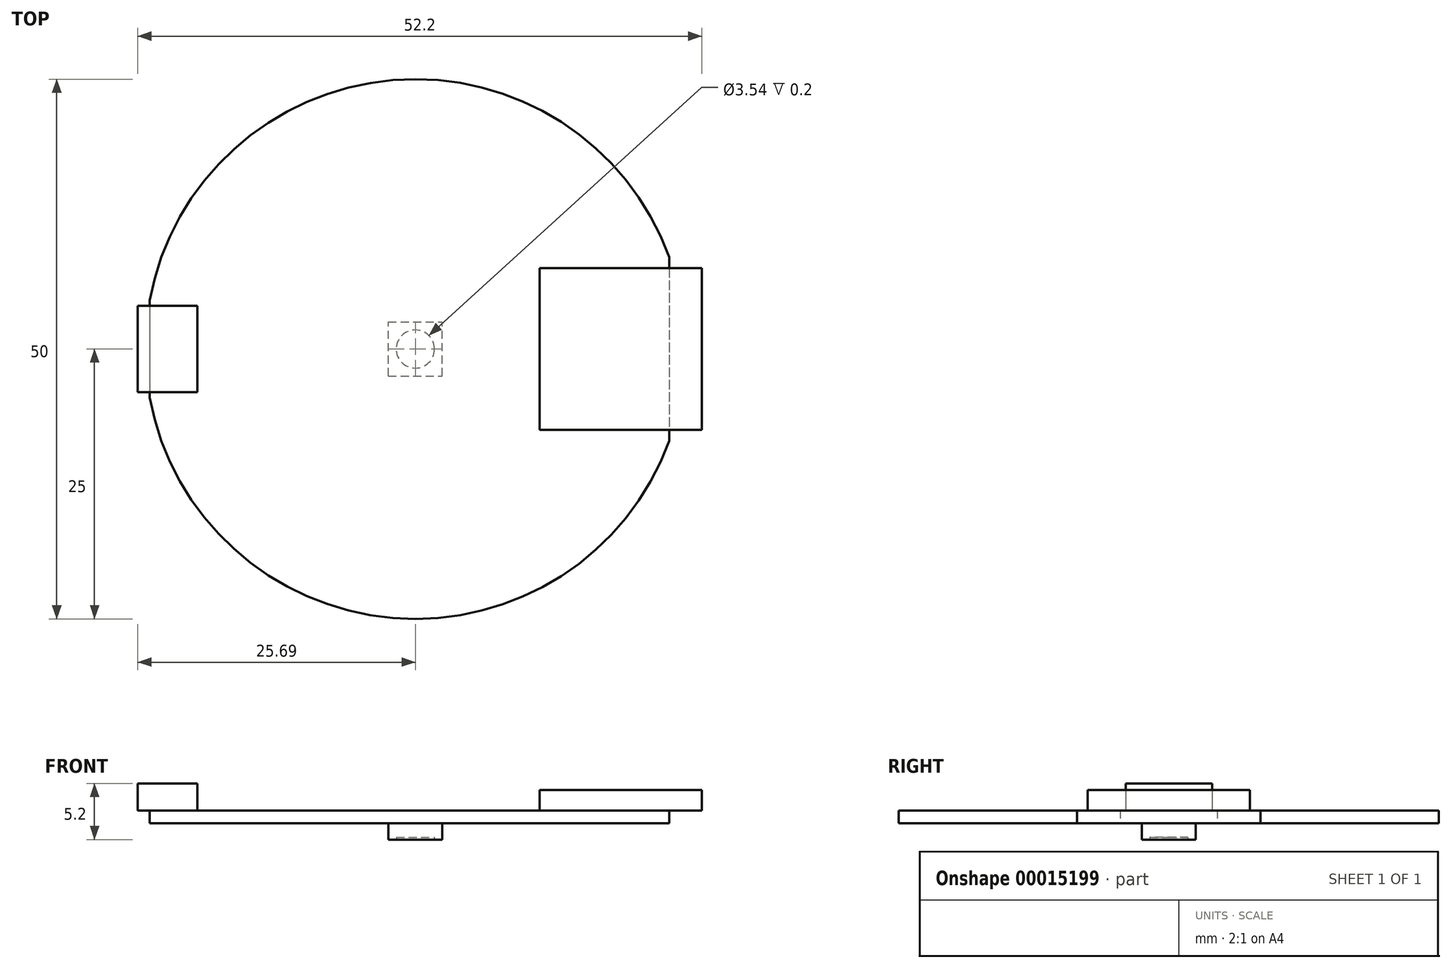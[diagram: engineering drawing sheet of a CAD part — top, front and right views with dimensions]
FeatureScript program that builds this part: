
annotation { "Feature Type Name" : "Feature", "Feature Type Description" : "" }
export const myFeature = defineFeature(function(context is Context, id is Id, definition is map)
    precondition{}
    {
        {
            var Q0;
            Q0=qCreatedBy(makeId("Top.planeOp"),FACE);
            var sketch = newSketch(context, id + "F0", { "sketchPlane" : qUnion([Q0])});
            skCircle(sketch, "E0", {"center": v(0, 0) * mm, "radius": 25 * mm});
            skLineSegment(sketch, "E1", {"start": v(23.51, 8.5) * mm, "end": v(23.51, -8.5) * mm});
            skLineSegment(sketch, "E2", {"start": v(-24.6, 4.5) * mm, "end": v(-24.6, -4.5) * mm});
            skSolve(sketch);
        }
        {
            var Q0;
            {var subQ0=sQuery(id+"F0.wireOp",EDGE,"E1");Q0=makeQuery(id+"F0.imprint","IMPRINT",FACE,{"disambiguationData":[TD([[makeQuery(id+"F0.imprint","IMPRINT",EDGE,{"derivedFrom":subQ0}),-1.0]])]});}
            extrude(context, id + "F1", {"entities" : qUnion([Q0]), "depth" : 1.2 * mm});
        }
        {
            var Q0;
            Q0=makeQuery(id+"F1.opExtrude","CAP_FACE",FACE,{"disambiguationData":[OSD([sQuery(id+"F0.wireOp",EDGE,"E0"),sQuery(id+"F0.wireOp",EDGE,"E1"),sQuery(id+"F0.wireOp",EDGE,"E2")])],"isStart":false});
            var sketch = newSketch(context, id + "F2", { "sketchPlane" : qUnion([Q0])});
            skLineSegment(sketch, "E3", {"start": v(0, 0) * mm, "end": v(-54.47, 0) * mm, "construction": true});
            skLineSegment(sketch, "E4.rect.bottom", {"start": v(-25.7, -4) * mm, "end": v(-20.2, -4) * mm});
            skLineSegment(sketch, "E4.rect.top", {"start": v(-25.7, 4) * mm, "end": v(-20.2, 4) * mm});
            skLineSegment(sketch, "E4.rect.left", {"start": v(-25.7, -4) * mm, "end": v(-25.7, 4) * mm});
            skLineSegment(sketch, "E4.rect.right", {"start": v(-20.2, -4) * mm, "end": v(-20.2, 4) * mm});
            skPoint(sketch, "E4.rect.middle", {"position": v(-22.94, 0) * mm});
            skPoint(sketch, "E5", {"position": v(-24.6, 0) * mm});
            skSolve(sketch);
        }
        {
            var Q0;
            Q0=qSketchRegion(id+"F2",true);
            extrude(context, id + "F3", {"entities" : qUnion([Q0]), "depth" : 2.5 * mm});
        }
        {
            var Q0;
            Q0=makeQuery(id+"F1.opExtrude","CAP_FACE",FACE,{"disambiguationData":[OSD([sQuery(id+"F0.wireOp",EDGE,"E0"),sQuery(id+"F0.wireOp",EDGE,"E1"),sQuery(id+"F0.wireOp",EDGE,"E2")])],"isStart":false});
            var sketch = newSketch(context, id + "F4", { "sketchPlane" : qUnion([Q0])});
            skLineSegment(sketch, "E6.bottom", {"start": v(26.51, -7.5) * mm, "end": v(11.51, -7.5) * mm});
            skLineSegment(sketch, "E6.top", {"start": v(26.51, 7.5) * mm, "end": v(11.51, 7.5) * mm});
            skLineSegment(sketch, "E6.left", {"start": v(26.51, -7.5) * mm, "end": v(26.51, 7.5) * mm});
            skLineSegment(sketch, "E6.right", {"start": v(11.51, -7.5) * mm, "end": v(11.51, 7.5) * mm});
            skLineSegment(sketch, "E7", {"start": v(0, 0) * mm, "end": v(28.6, 0) * mm, "construction": true});
            skSolve(sketch);
        }
        {
            var Q0;
            Q0=qSketchRegion(id+"F4",true);
            extrude(context, id + "F5", {"entities" : qUnion([Q0]), "depth" : 1.9 * mm});
        }
        {
            var Q0;
            Q0=makeQuery(id+"F1.opExtrude","CAP_FACE",FACE,{"disambiguationData":[OSD([sQuery(id+"F0.wireOp",EDGE,"E0"),sQuery(id+"F0.wireOp",EDGE,"E1"),sQuery(id+"F0.wireOp",EDGE,"E2")])],"isStart":true});
            var sketch = newSketch(context, id + "F6", { "sketchPlane" : qUnion([Q0])});
            skLineSegment(sketch, "E8.rect.bottom", {"start": v(-2.5, 2.5) * mm, "end": v(2.5, 2.5) * mm});
            skLineSegment(sketch, "E8.rect.top", {"start": v(-2.5, -2.5) * mm, "end": v(2.5, -2.5) * mm});
            skLineSegment(sketch, "E8.rect.left", {"start": v(-2.5, 2.5) * mm, "end": v(-2.5, -2.5) * mm});
            skLineSegment(sketch, "E8.rect.right", {"start": v(2.5, 2.5) * mm, "end": v(2.5, -2.5) * mm});
            skPoint(sketch, "E8.rect.middle", {"position": v(0, 0) * mm});
            skCircle(sketch, "E9", {"center": v(0, 0) * mm, "radius": 1.75 * mm});
            skSolve(sketch);
        }
        {
            var Q0;
            Q0=makeQuery(id+"F6.imprint","IMPRINT",FACE,{"disambiguationData":[TD([[makeQuery(id+"F6.imprint","IMPRINT",EDGE,{"derivedFrom":sQuery(id+"F6.wireOp",EDGE,"E8.rect.bottom")}),-1.0]])]});
            var Q1;
            Q1=makeQuery(id+"F6.imprint","IMPRINT",FACE,{"disambiguationData":[TD([[makeQuery(id+"F6.imprint","IMPRINT",EDGE,{"derivedFrom":sQuery(id+"F6.wireOp",EDGE,"E9")}),1.0]])]});
            extrude(context, id + "F7", {"entities" : qUnion([Q0, Q1]), "depth" : 1.5 * mm});
        }
        {
            var Q0;
            Q0=makeQuery(id+"F7.opExtrude","CAP_FACE",FACE,{"disambiguationData":[OSD([sQuery(id+"F6.wireOp",EDGE,"E8.rect.bottom"),sQuery(id+"F6.wireOp",EDGE,"E8.rect.top"),sQuery(id+"F6.wireOp",EDGE,"E8.rect.left"),sQuery(id+"F6.wireOp",EDGE,"E8.rect.right")])],"isStart":false});
            var sketch = newSketch(context, id + "F8", { "sketchPlane" : qUnion([Q0])});
            skCircle(sketch, "E10", {"center": v(0, 0) * mm, "radius": 1.77 * mm});
            skSolve(sketch);
        }
        {
            var Q0;
            Q0=qSketchRegion(id+"F8",true);
            extrude(context, id + "F9", {"entities" : qUnion([Q0]), "operationType" : NewBodyOperationType.REMOVE, "oppositeDirection" : true, "depth" : .2 * mm});
        }
    });
